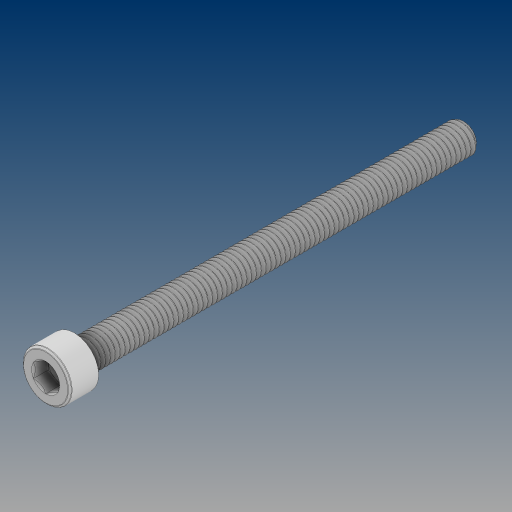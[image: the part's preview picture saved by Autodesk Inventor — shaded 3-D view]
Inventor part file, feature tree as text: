
AUTODESK INVENTOR PART (.ipt)
format: ipt  version: 2024.3 (Build 283343000, 343)  size: 1,710,080 bytes
history: native  units: in
note: dims shown in document units (in); Inventor stores cm internally (conversion verified against a paired STEP export)
features: revolve x1
ambient origin geometry x8: Origin, YZ Plane, XZ Plane, XY Plane, X Axis, Y Axis, Z Axis, Center Point
bodies: Solid1 (feature_tree)
feature tree (1):
  revolve  "Revolve2"  [1 undecoded]
note: 1 required parameter value undecoded (feature->parameter linkage not recoverable at this tier; creation-order binding heuristic only, values carry confidence <= 0.55)
